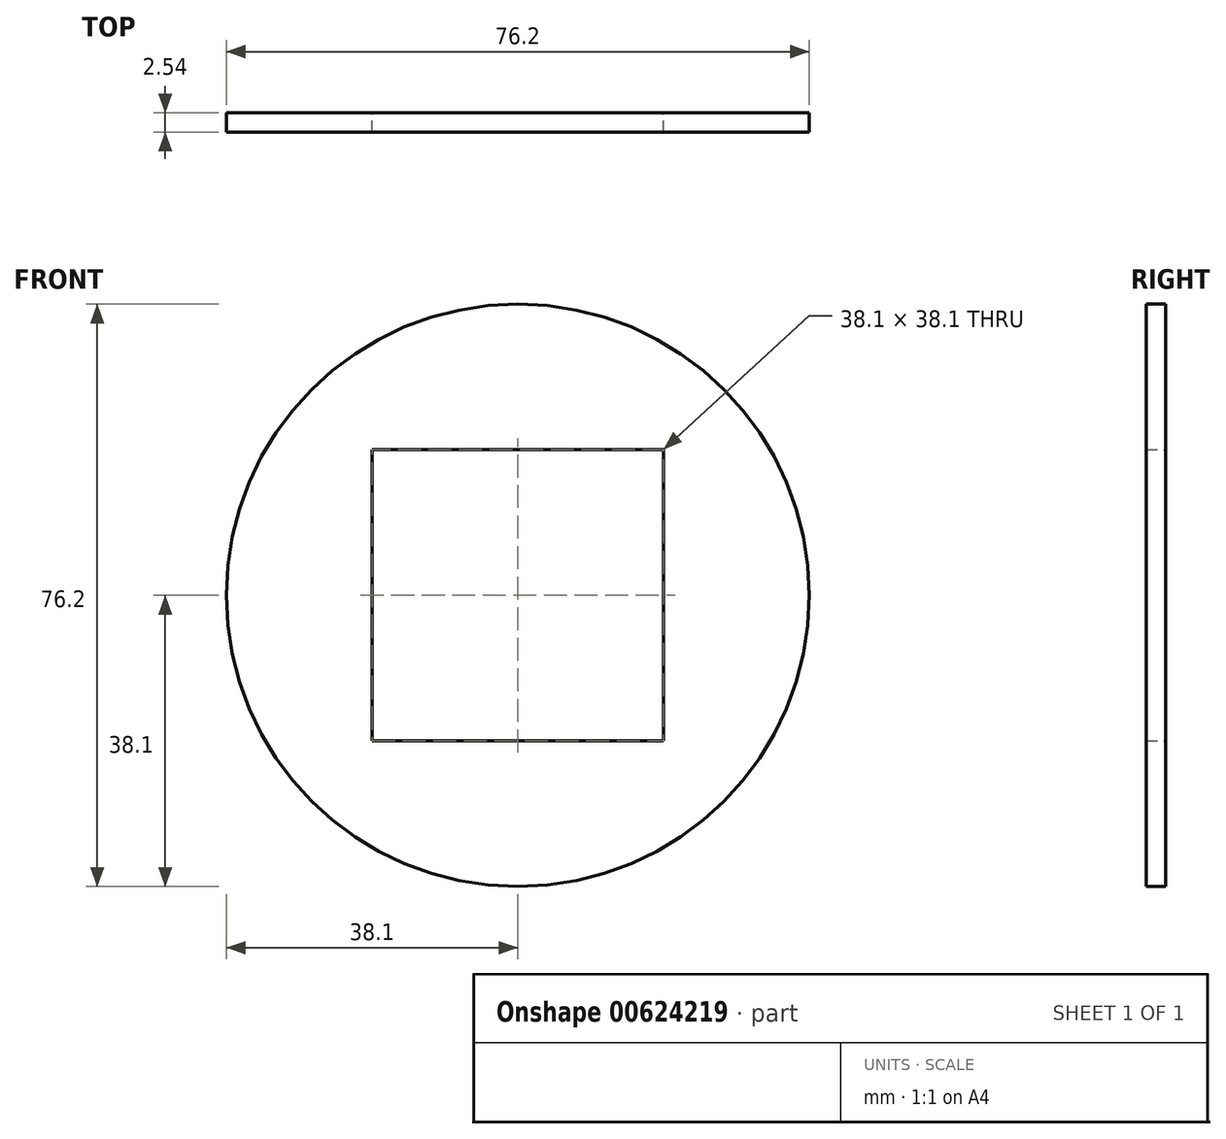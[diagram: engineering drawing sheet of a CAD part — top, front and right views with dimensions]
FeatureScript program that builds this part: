
annotation { "Feature Type Name" : "Feature", "Feature Type Description" : "" }
export const myFeature = defineFeature(function(context is Context, id is Id, definition is map)
    precondition{}
    {
        {
            var Q0;
            Q0=qCreatedBy(makeId("Front.planeOp"),FACE);
            var sketch = newSketch(context, id + "F0", { "sketchPlane" : qUnion([Q0])});
            skCircle(sketch, "E0", {"center": v(0, 0) * mm, "radius": 38.1 * mm});
            skLineSegment(sketch, "E1.bottom", {"start": v(-19.05, -19.05) * mm, "end": v(19.05, -19.05) * mm});
            skLineSegment(sketch, "E1.top", {"start": v(-19.05, 19.05) * mm, "end": v(19.05, 19.05) * mm});
            skLineSegment(sketch, "E1.left", {"start": v(-19.05, -19.05) * mm, "end": v(-19.05, 19.05) * mm});
            skLineSegment(sketch, "E1.right", {"start": v(19.05, -19.05) * mm, "end": v(19.05, 19.05) * mm});
            skSolve(sketch);
        }
        {
            var Q0;
            Q0=makeQuery(id+"F0.imprint","IMPRINT",FACE,{"disambiguationData":[TD([[makeQuery(id+"F0.imprint","IMPRINT",EDGE,{"derivedFrom":sQuery(id+"F0.wireOp",EDGE,"E0")}),1.0]])]});
            extrude(context, id + "F1", {"entities" : qUnion([Q0]), "depth" : 2.54 * mm, "offsetDistance" : 25.4 * mm});
        }
    });
